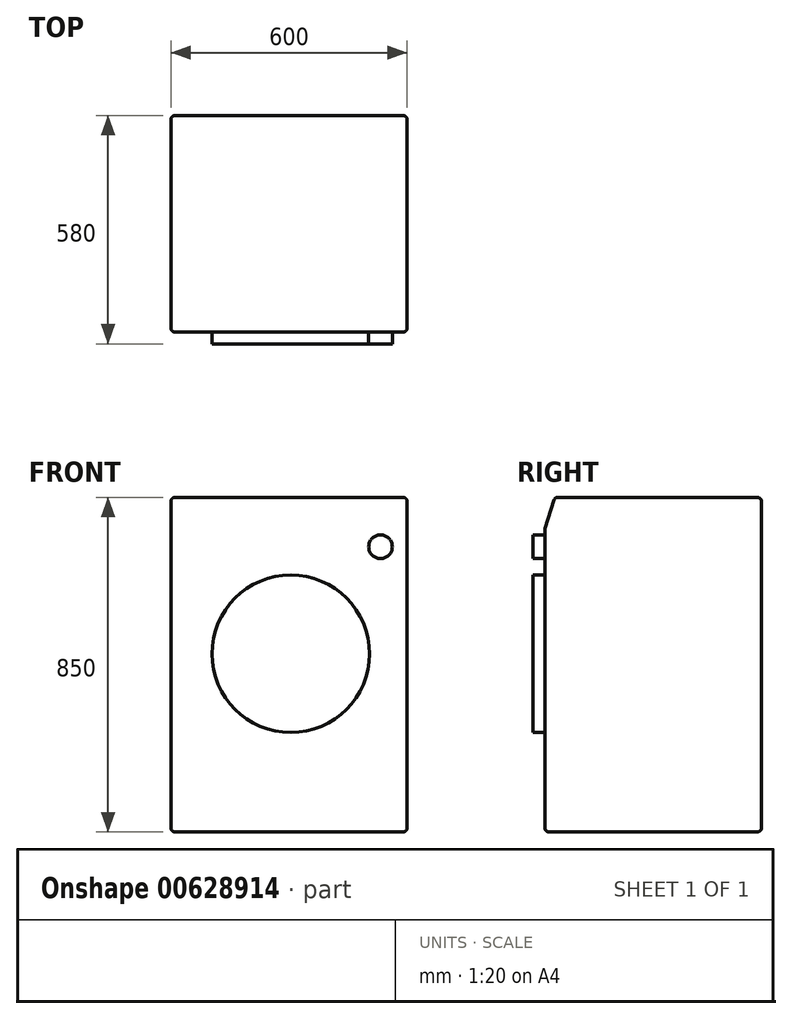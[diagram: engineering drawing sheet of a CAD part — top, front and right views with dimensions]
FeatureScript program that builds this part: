
annotation { "Feature Type Name" : "Feature", "Feature Type Description" : "" }
export const myFeature = defineFeature(function(context is Context, id is Id, definition is map)
    precondition{}
    {
        {
            var Q0;
            Q0=qCreatedBy(makeId("Front.planeOp"),FACE);
            var sketch = newSketch(context, id + "F0", { "sketchPlane" : qUnion([Q0])});
            skLineSegment(sketch, "E0.bottom", {"start": v(0, 0) * mm, "end": v(600, 0) * mm});
            skLineSegment(sketch, "E0.top", {"start": v(0, 850) * mm, "end": v(600, 850) * mm});
            skLineSegment(sketch, "E0.left", {"start": v(0, 0) * mm, "end": v(0, 850) * mm});
            skLineSegment(sketch, "E0.right", {"start": v(600, 0) * mm, "end": v(600, 850) * mm});
            skSolve(sketch);
        }
        {
            var Q0;
            Q0=makeQuery(id+"F0.imprint","IMPRINT",FACE,{"disambiguationData":[TD([[makeQuery(id+"F0.imprint","IMPRINT",EDGE,{"derivedFrom":sQuery(id+"F0.wireOp",EDGE,"E0.bottom")}),1.0]])]});
            extrude(context, id + "F1", {"entities" : qUnion([Q0]), "depth" : 550 * mm, "offsetDistance" : 25 * mm});
        }
        {
            var Q0;
            Q0=makeQuery(id+"F1.opExtrude","CAP_EDGE",EDGE,{"disambiguationData":[OSD([sQuery(id+"F0.wireOp",EDGE,"E0.top")])],"isStart":false});
            chamfer(context, id + "F2", {"entities" : qUnion([Q0]), "chamferType" : ChamferType.TWO_OFFSETS, "width1" : 25 * mm, "oppositeDirection" : false, "width2" : 80 * mm, "tangentPropagation" : true});
        }
        {
            var Q0;
            Q0=makeQuery(id+"F1.opExtrude","CAP_EDGE",EDGE,{"disambiguationData":[OSD([sQuery(id+"F0.wireOp",EDGE,"E0.left")])],"isStart":false});
            var Q1;
            Q1=makeQuery(id+"F1.opExtrude","CAP_EDGE",EDGE,{"disambiguationData":[OSD([sQuery(id+"F0.wireOp",EDGE,"E0.left")])],"isStart":true});
            var Q2;
            Q2=makeQuery(id+"F1.opExtrude","CAP_EDGE",EDGE,{"disambiguationData":[OSD([sQuery(id+"F0.wireOp",EDGE,"E0.right")])],"isStart":false});
            var Q3;
            Q3=makeQuery(id+"F1.opExtrude","CAP_EDGE",EDGE,{"disambiguationData":[OSD([sQuery(id+"F0.wireOp",EDGE,"E0.right")])],"isStart":true});
            var Q4;
            Q4=makeQuery(id+"F1.opExtrude","SWEPT_EDGE",EDGE,{"disambiguationData":[OSD([sQuery(id+"F0.wireOp",EDGE,"E0.bottom"),sQuery(id+"F0.wireOp",EDGE,"E0.left")])]});
            var Q5;
            {var subQ0=sQuery(id+"F0.wireOp",EDGE,"E0.top");Q5=makeQuery(id+"F2.opChamfer","BLEND_EDGE",EDGE,{"blendedFrom":[makeQuery(id+"F1.opExtrude","CAP_EDGE",EDGE,{"disambiguationData":[OSD([subQ0])],"isStart":false}),makeQuery(id+"F1.opExtrude","SWEPT_FACE",FACE,{"disambiguationData":[OSD([subQ0])]})],"blendedInto":[makeQuery(id+"F1.opExtrude","SWEPT_FACE",FACE,{"disambiguationData":[OSD([subQ0])]})]});}
            var Q6;
            {var subQ0=sQuery(id+"F0.wireOp",EDGE,"E0.top");Q6=makeQuery(id+"F2.opChamfer","BLEND_EDGE",EDGE,{"blendedFrom":[makeQuery(id+"F1.opExtrude","CAP_EDGE",EDGE,{"disambiguationData":[OSD([subQ0])],"isStart":false}),makeQuery(id+"F1.opExtrude","CAP_FACE",FACE,{"disambiguationData":[OSD([sQuery(id+"F0.wireOp",EDGE,"E0.bottom"),subQ0,sQuery(id+"F0.wireOp",EDGE,"E0.left"),sQuery(id+"F0.wireOp",EDGE,"E0.right")])],"isStart":false})],"blendedInto":[makeQuery(id+"F1.opExtrude","CAP_FACE",FACE,{"disambiguationData":[OSD([sQuery(id+"F0.wireOp",EDGE,"E0.bottom"),subQ0,sQuery(id+"F0.wireOp",EDGE,"E0.left"),sQuery(id+"F0.wireOp",EDGE,"E0.right")])],"isStart":false})]});}
            var Q7;
            Q7=makeQuery(id+"F1.opExtrude","SWEPT_EDGE",EDGE,{"disambiguationData":[OSD([sQuery(id+"F0.wireOp",EDGE,"E0.top"),sQuery(id+"F0.wireOp",EDGE,"E0.right")])]});
            var Q8;
            Q8=makeQuery(id+"F1.opExtrude","SWEPT_EDGE",EDGE,{"disambiguationData":[OSD([sQuery(id+"F0.wireOp",EDGE,"E0.top"),sQuery(id+"F0.wireOp",EDGE,"E0.left")])]});
            var Q9;
            Q9=makeQuery(id+"F1.opExtrude","SWEPT_EDGE",EDGE,{"disambiguationData":[OSD([sQuery(id+"F0.wireOp",EDGE,"E0.bottom"),sQuery(id+"F0.wireOp",EDGE,"E0.right")])]});
            var Q10;
            Q10=makeQuery(id+"F2.opChamfer","BLEND_EDGE",EDGE,{"blendedFrom":[makeQuery(id+"F1.opExtrude","CAP_EDGE",EDGE,{"disambiguationData":[OSD([sQuery(id+"F0.wireOp",EDGE,"E0.top")])],"isStart":false}),makeQuery(id+"F1.opExtrude","SWEPT_FACE",FACE,{"disambiguationData":[OSD([sQuery(id+"F0.wireOp",EDGE,"E0.right")])]})],"blendedInto":[makeQuery(id+"F1.opExtrude","SWEPT_FACE",FACE,{"disambiguationData":[OSD([sQuery(id+"F0.wireOp",EDGE,"E0.right")])]})]});
            var Q11;
            Q11=makeQuery(id+"F1.opExtrude","CAP_EDGE",EDGE,{"disambiguationData":[OSD([sQuery(id+"F0.wireOp",EDGE,"E0.bottom")])],"isStart":false});
            var Q12;
            Q12=makeQuery(id+"F2.opChamfer","BLEND_EDGE",EDGE,{"blendedFrom":[makeQuery(id+"F1.opExtrude","CAP_EDGE",EDGE,{"disambiguationData":[OSD([sQuery(id+"F0.wireOp",EDGE,"E0.top")])],"isStart":false}),makeQuery(id+"F1.opExtrude","SWEPT_FACE",FACE,{"disambiguationData":[OSD([sQuery(id+"F0.wireOp",EDGE,"E0.left")])]})],"blendedInto":[makeQuery(id+"F1.opExtrude","SWEPT_FACE",FACE,{"disambiguationData":[OSD([sQuery(id+"F0.wireOp",EDGE,"E0.left")])]})]});
            var Q13;
            Q13=makeQuery(id+"F1.opExtrude","CAP_EDGE",EDGE,{"disambiguationData":[OSD([sQuery(id+"F0.wireOp",EDGE,"E0.bottom")])],"isStart":true});
            var Q14;
            Q14=makeQuery(id+"F1.opExtrude","CAP_EDGE",EDGE,{"disambiguationData":[OSD([sQuery(id+"F0.wireOp",EDGE,"E0.top")])],"isStart":true});
            fillet(context, id + "F3", {"entities" : qUnion([Q0, Q1, Q2, Q3, Q4, Q5, Q6, Q7, Q8, Q9, Q10, Q11, Q12, Q13, Q14]), "radius" : 10 * mm, "tangentPropagation" : true, "allowEdgeOverflow" : false});
        }
        {
            var Q0;
            Q0=makeQuery(id+"F1.opExtrude","CAP_FACE",FACE,{"disambiguationData":[OSD([sQuery(id+"F0.wireOp",EDGE,"E0.bottom"),sQuery(id+"F0.wireOp",EDGE,"E0.top"),sQuery(id+"F0.wireOp",EDGE,"E0.left"),sQuery(id+"F0.wireOp",EDGE,"E0.right")])],"isStart":false});
            var sketch = newSketch(context, id + "F4", { "sketchPlane" : qUnion([Q0])});
            skCircle(sketch, "E1", {"center": v(304.43, 452.61) * mm, "radius": 200 * mm});
            skCircle(sketch, "E2", {"center": v(532.35, 724.46) * mm, "radius": 30 * mm});
            skSolve(sketch);
        }
        {
            var Q0;
            Q0=makeQuery(id+"F4.imprint","IMPRINT",FACE,{"disambiguationData":[TD([[makeQuery(id+"F4.imprint","IMPRINT",EDGE,{"derivedFrom":sQuery(id+"F4.wireOp",EDGE,"E1")}),1.0]])]});
            extrude(context, id + "F5", {"entities" : qUnion([Q0]), "operationType" : NewBodyOperationType.ADD, "depth" : 30 * mm, "offsetDistance" : 25 * mm});
        }
        {
            var Q0;
            Q0=makeQuery(id+"F4.imprint","IMPRINT",FACE,{"disambiguationData":[TD([[makeQuery(id+"F4.imprint","IMPRINT",EDGE,{"derivedFrom":sQuery(id+"F4.wireOp",EDGE,"E2")}),1.0]])]});
            extrude(context, id + "F6", {"entities" : qUnion([Q0]), "operationType" : NewBodyOperationType.ADD, "depth" : 30 * mm, "offsetDistance" : 25 * mm});
        }
    });
